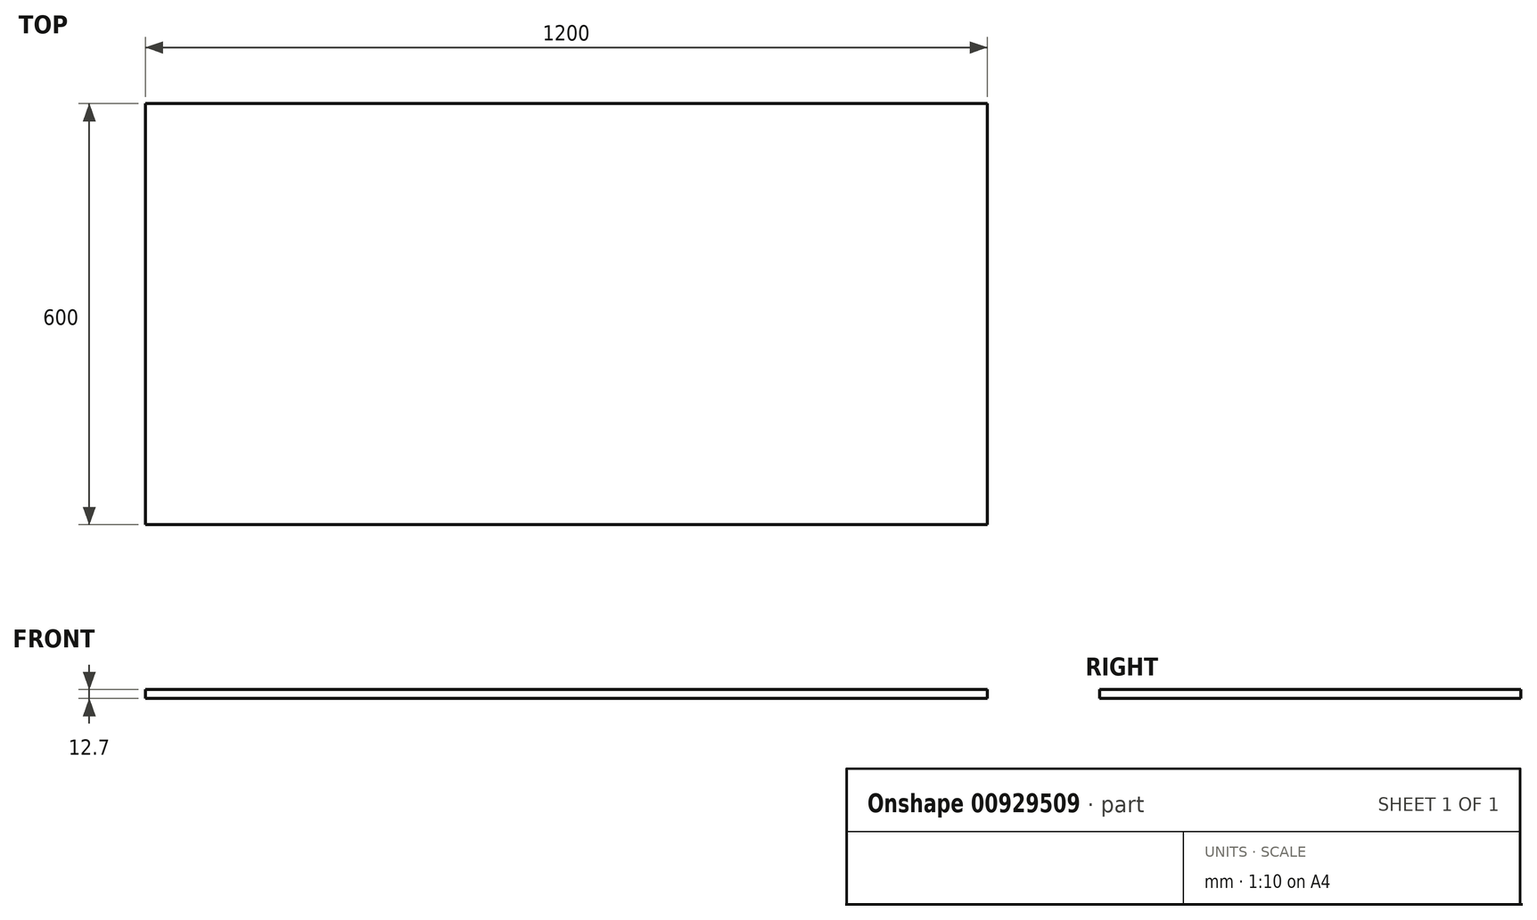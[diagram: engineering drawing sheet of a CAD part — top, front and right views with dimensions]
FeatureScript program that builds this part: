
annotation { "Feature Type Name" : "Feature", "Feature Type Description" : "" }
export const myFeature = defineFeature(function(context is Context, id is Id, definition is map)
    precondition{}
    {
        {
            var Q0;
            Q0=qCreatedBy(makeId("Front.planeOp"),FACE);
            var sketch = newSketch(context, id + "F0", { "sketchPlane" : qUnion([Q0])});
            skLineSegment(sketch, "E0", {"start": v(0, 0) * mm, "end": v(600, 0) * mm});
            skLineSegment(sketch, "E1", {"start": v(0, 0) * mm, "end": v(-600, 0) * mm});
            skLineSegment(sketch, "E2", {"start": v(-600, 0) * mm, "end": v(-600, 12.7) * mm});
            skLineSegment(sketch, "E3", {"start": v(600, 0) * mm, "end": v(600, 12.7) * mm});
            skLineSegment(sketch, "E4", {"start": v(-600, 12.7) * mm, "end": v(600, 12.7) * mm});
            skSolve(sketch);
        }
        {
            var Q0;
            Q0=makeQuery(id+"F0.imprint","IMPRINT",FACE,{"disambiguationData":[TD([[makeQuery(id+"F0.imprint","IMPRINT",EDGE,{"derivedFrom":sQuery(id+"F0.wireOp",EDGE,"E0")}),1.0]])]});
            extrude(context, id + "F1", {"entities" : qUnion([Q0]), "endBound" : BoundingType.SYMMETRIC, "depth" : 600 * mm, "offsetDistance" : 25 * mm});
        }
    });
